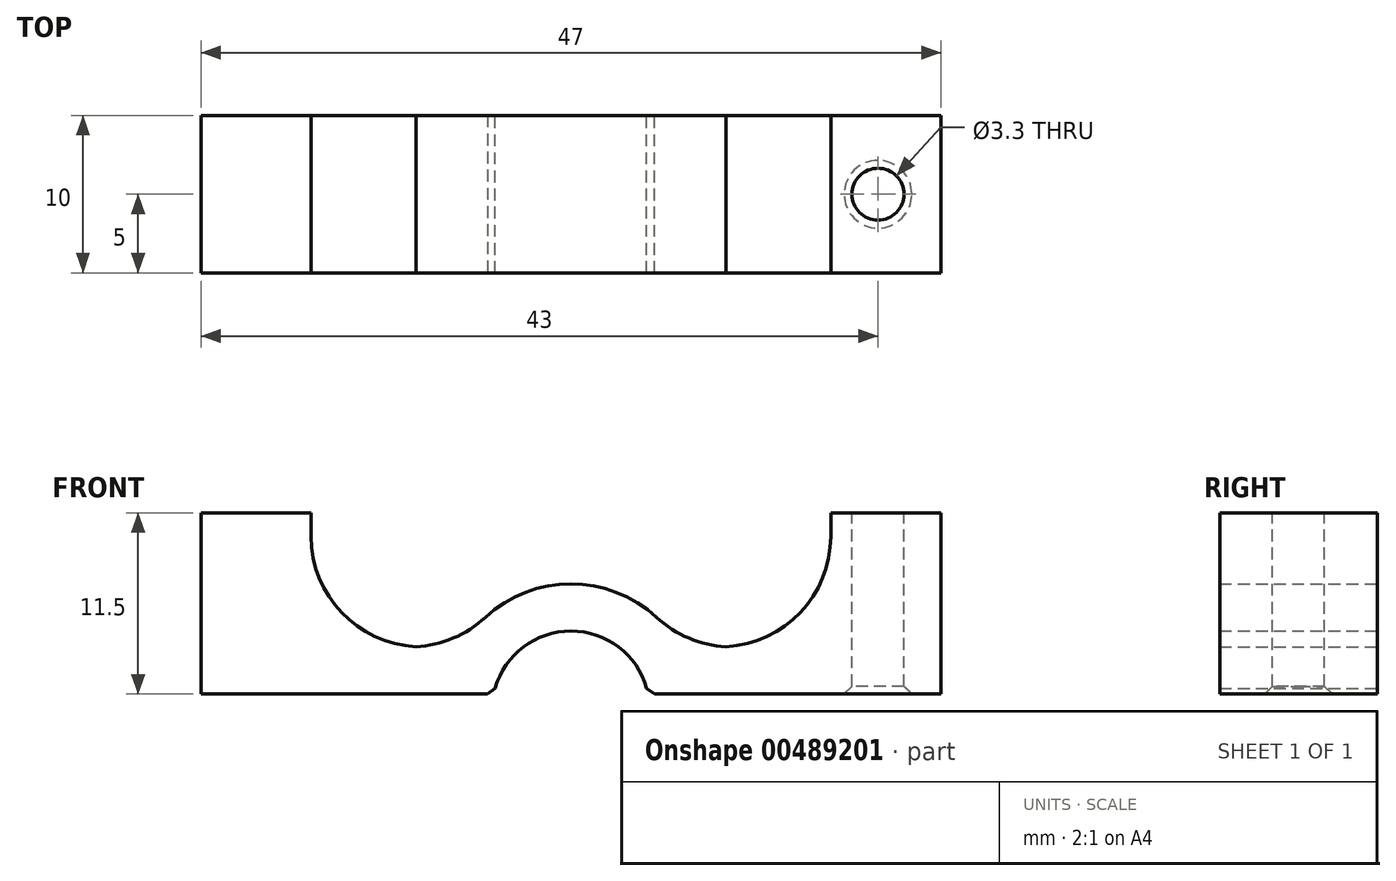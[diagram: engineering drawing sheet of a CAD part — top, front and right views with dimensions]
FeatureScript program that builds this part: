
annotation { "Feature Type Name" : "Feature", "Feature Type Description" : "" }
export const myFeature = defineFeature(function(context is Context, id is Id, definition is map)
    precondition{}
    {
        {
            var Q0;
            Q0=qCreatedBy(makeId("Front.planeOp"),FACE);
            var sketch = newSketch(context, id + "F0", { "sketchPlane" : qUnion([Q0])});
            skLineSegment(sketch, "E0", {"start": v(0, 11) * mm, "end": v(0, -24.49) * mm, "construction": true});
            skLineSegment(sketch, "E1", {"start": v(23.5, 1) * mm, "end": v(23.5, 12.5) * mm});
            skLineSegment(sketch, "E2", {"start": v(23.5, 12.5) * mm, "end": v(16.5, 12.5) * mm});
            skLineSegment(sketch, "E3", {"start": v(16.5, 12.5) * mm, "end": v(16.5, 4) * mm});
            skArc(sketch, "E4", {"start": v(4.9, 1) * mm, "mid": v(3.16, 3.87) * mm, "end": v(0, 5) * mm});
            skLineSegment(sketch, "E5", {"start": v(4.9, 1) * mm, "end": v(23.5, 1) * mm});
            skLineSegment(sketch, "E6.MirrorCS", {"start": v(-4.9, 1) * mm, "end": v(-23.5, 1) * mm});
            skLineSegment(sketch, "E7.MirrorCS", {"start": v(-16.5, 12.5) * mm, "end": v(-16.5, 4) * mm});
            skLineSegment(sketch, "E8.MirrorCS", {"start": v(-23.5, 1) * mm, "end": v(-23.5, 12.5) * mm});
            skArc(sketch, "E9.MirrorCS", {"start": v(-4.9, 1) * mm, "mid": v(-3.16, 3.87) * mm, "end": v(0, 5) * mm});
            skLineSegment(sketch, "E10.MirrorCS", {"start": v(-23.5, 12.5) * mm, "end": v(-16.5, 12.5) * mm});
            skLineSegment(sketch, "E11.0", {"start": v(6.93, 4) * mm, "end": v(16.5, 4) * mm});
            skArc(sketch, "E12.0", {"start": v(6.93, 4) * mm, "mid": v(4, 6.93) * mm, "end": v(0, 8) * mm});
            skPoint(sketch, "E13.MirrorCS.end.orphan", {"position": v(0, 11) * mm});
            skArc(sketch, "E14.MirrorCS", {"start": v(-6.93, 4) * mm, "mid": v(-4, 6.93) * mm, "end": v(0, 8) * mm});
            skLineSegment(sketch, "E15.MirrorCS", {"start": v(-6.93, 4) * mm, "end": v(-16.5, 4) * mm});
            skSolve(sketch);
        }
        {
            var Q0;
            Q0 = qSketchRegion(id + "F0", true);
            extrude(context, id + "F1", {"entities" : qUnion([Q0]), "endBound" : BoundingType.SYMMETRIC, "depth" : 10 * mm});
        }
        {
            var Q0;
            Q0=makeQuery(id+"F1.opExtrude","SWEPT_EDGE",EDGE,{"disambiguationData":[OSD([sQuery(id+"F0.wireOp",EDGE,"E3"),sQuery(id+"F0.wireOp",EDGE,"E11.0")])]});
            var Q1;
            Q1=makeQuery(id+"F1.opExtrude","SWEPT_EDGE",EDGE,{"disambiguationData":[OSD([sQuery(id+"F0.wireOp",EDGE,"E11.0"),sQuery(id+"F0.wireOp",EDGE,"E12.0")])]});
            var Q2;
            Q2=makeQuery(id+"F1.opExtrude","SWEPT_EDGE",EDGE,{"disambiguationData":[OSD([sQuery(id+"F0.wireOp",EDGE,"E14.MirrorCS"),sQuery(id+"F0.wireOp",EDGE,"E15.MirrorCS")])]});
            var Q3;
            Q3=makeQuery(id+"F1.opExtrude","SWEPT_EDGE",EDGE,{"disambiguationData":[OSD([sQuery(id+"F0.wireOp",EDGE,"E7.MirrorCS"),sQuery(id+"F0.wireOp",EDGE,"E15.MirrorCS")])]});
            fillet(context, id + "F2", {"entities" : qUnion([Q0, Q1, Q2, Q3]), "radius" : 7 * mm, "tangentPropagation" : true, "allowEdgeOverflow" : false});
        }
        {
            var Q0;
            Q0=makeQuery(id+"F1.opExtrude","SWEPT_EDGE",EDGE,{"disambiguationData":[OSD([sQuery(id+"F0.wireOp",EDGE,"E6.MirrorCS"),sQuery(id+"F0.wireOp",EDGE,"E9.MirrorCS")])]});
            var Q1;
            Q1=makeQuery(id+"F1.opExtrude","SWEPT_EDGE",EDGE,{"disambiguationData":[OSD([sQuery(id+"F0.wireOp",EDGE,"E4"),sQuery(id+"F0.wireOp",EDGE,"E5")])]});
            chamfer(context, id + "F3", {"entities" : qUnion([Q0, Q1]), "width" : 0.5 * mm, "tangentPropagation" : true});
        }
        {
            var Q0;
            Q0=makeQuery(id+"F1.opExtrude","SWEPT_FACE",FACE,{"disambiguationData":[OSD([sQuery(id+"F0.wireOp",EDGE,"E2")])]});
            var sketch = newSketch(context, id + "F4", { "sketchPlane" : qUnion([Q0])});
            skCircle(sketch, "E16", {"center": v(19.5, 0) * mm, "radius": 1.65 * mm});
            skPoint(sketch, "E17", {"position": v(23.5, 0) * mm});
            skLineSegment(sketch, "E18", {"start": v(0, 0) * mm, "end": v(0, -5) * mm, "construction": true});
            skSolve(sketch);
        }
        {
            var Q0;
            Q0 = qSketchRegion(id + "F4", true);
            extrude(context, id + "F5", {"entities" : qUnion([Q0]), "operationType" : NewBodyOperationType.REMOVE, "endBound" : BoundingType.THROUGH_ALL, "oppositeDirection" : true, "depth" : 25 * mm});
        }
        {
            var Q0;
            Q0=makeQuery(id+"F5.boolean.opBoolean","COPY",EDGE,{"derivedFrom":makeQuery(id+"F5.opExtrude","CAP_EDGE",EDGE,{"disambiguationData":[OSD([sQuery(id+"F4.wireOp",EDGE,"E16")])],"isStart":true})});
            var Q1;
            Q1=makeQuery(id+"FrH7mDHGo6yiDWq_1.1.F5.boolean.opBoolean","COPY",EDGE,{"derivedFrom":makeQuery(id+"FrH7mDHGo6yiDWq_1.1.F5.opExtrude","CAP_EDGE",EDGE,{"disambiguationData":[OSD([sQuery(id+"F4.wireOp",EDGE,"E16")])],"isStart":true})});
            var Q2;
            Q2=makeQuery(id+"F5.boolean.opBoolean","INTERSECT",EDGE,{"derivedFrom":[makeQuery(id+"F1.opExtrude","SWEPT_FACE",FACE,{"disambiguationData":[OSD([sQuery(id+"F0.wireOp",EDGE,"E5")])]}),makeQuery(id+"F5.opExtrude","SWEPT_FACE",FACE,{"disambiguationData":[OSD([sQuery(id+"F4.wireOp",EDGE,"E16")])]})]});
            var Q3;
            Q3=makeQuery(id+"FrH7mDHGo6yiDWq_1.1.F5.boolean.opBoolean","INTERSECT",EDGE,{"derivedFrom":[makeQuery(id+"F1.opExtrude","SWEPT_FACE",FACE,{"disambiguationData":[OSD([sQuery(id+"F0.wireOp",EDGE,"E6.MirrorCS")])]}),makeQuery(id+"FrH7mDHGo6yiDWq_1.1.F5.opExtrude","SWEPT_FACE",FACE,{"disambiguationData":[OSD([sQuery(id+"F4.wireOp",EDGE,"E16")])]})]});
            chamfer(context, id + "F6", {"entities" : qUnion([Q0, Q1, Q2, Q3]), "width" : 0.5 * mm, "tangentPropagation" : true});
        }
    });
